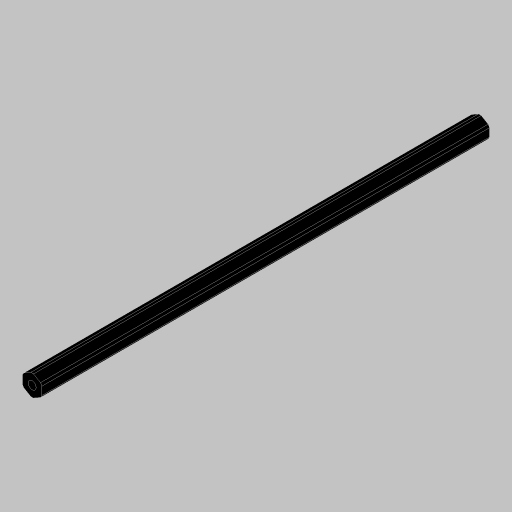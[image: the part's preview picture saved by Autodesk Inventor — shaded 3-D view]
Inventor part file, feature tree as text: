
AUTODESK INVENTOR PART (.ipt)
format: ipt  version: 2023.5 (Build 275446000, 446)  size: 119,808 bytes
history: native  units: in
note: dims shown in document units (in); Inventor stores cm internally (conversion verified against a paired STEP export)
features: extrude x2, projected_geometry x2, hole x1
ambient origin geometry x8: Origin, YZ Plane, XZ Plane, XY Plane, X Axis, Y Axis, Z Axis, Center Point
bodies: Solid1 (feature_tree)
feature tree (5):
  extrude  "Extrusion1"  TaperAngle=0.0deg  [1 undecoded]
  hole  "Hole1"  [1 undecoded]
  extrude  "Extrusion3"  TaperAngle=0.0deg  [1 undecoded]
  projected_geometry  "Project Cut Edges1"
  projected_geometry  "Project Cut Edges2"
note: 3 required parameter values undecoded (feature->parameter linkage not recoverable at this tier; creation-order binding heuristic only, values carry confidence <= 0.55)
